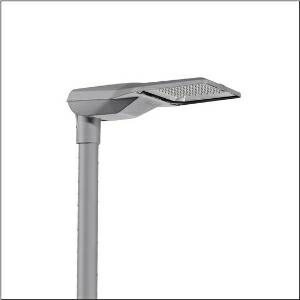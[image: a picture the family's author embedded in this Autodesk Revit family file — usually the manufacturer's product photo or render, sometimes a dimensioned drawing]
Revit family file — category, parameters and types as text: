
# Revit family: streetlight_sl_21_iq_midi___st0_8a_5xe3c41d08mb_0a8a
name_source: partatom
category: Lighting Fixtures
units: mm (PartAtom-declared; Revit-internal decimal feet)

## family parameters
Cut with Voids When Loaded = No
Host = Face
Light Source = No
Part Type = Normal
Room Calculation Point = No
Round Connector Dimension = Use Diameter
Shared = No

## types (1)
- --- (1 x LED, 20360 lm, 146.7 W, 4000K)
    Apparent Load = 147 VA
    CIE Flux Codes = 38 75 97 100 100
    Color Rendering = 70
    Color Temperature = 4000K
    Default Elevation = 1800 mm
    Description = Streetlight SL 21 iQ midi, mast luminaire, primary light control with lens, of PMMA, primary optical cover: cover, of toughened safety glass, transparent, light distribution: ST0.8a, light emission: direct distribution, primary light characteristic: asymmetric, installation type: post-top, side-entry, LED, High Power LED, rated luminous flux: 20.360lm, luminous efficacy: 139lm/W, light colour: 740, colour temperature: 4000K, control gear: iQ-Comfort, control: Auto-Match, Temp-Guard, Lumen-Switch, Night-Set, Smart-Wire, Light-Fading, Desk-Remote (wireless, voltage-free reading and setting of iQ features in the workshop via application-optimized NFC function/RFID function), optimised constant luminous flux control (CLO 2.0), pre-setting: linear dimming characteristic, mains connection: 230..240V, AC, 50/60Hz, start of lifetime: 147W, end of service life: 161W, reduction: 62W, luminaire housing, of diecast aluminium, powder-coated, Siteco® metallic grey (DB 702S), corrosivity category C5 mid according to DIN EN ISO 12944, please order mast flange separately, inclination adjustable: 0°, 5°, 10°, 15°, sealing non-destructively replaceable, multi-level sealing system, length: 644mm, width: 335mm, height: 110mm, mast flange for spigot size: 42mm (side-entry): 5XC10008XM4, 60/48mm (side-entry/post-top): 5XC10108XM2, 76/60mm (side-entry/post-top): 5XC10108XM1, mounting height: 4..8m, protection rating (complete): IP66, insulation class (complete): insulation class II (safety insulation), certification: CE, ENEC, ENEC+, VDE, impact resistance: IK10, permissible operating ambient temperature for outdoor applications: -40..+50°C, standard-compliant lighting for roads and squares, packaging unit: 1 piece

Light Distribution: ST0.8a
    Height = 111 mm
    Lamp = 1 x LED
    Lamp Light Flux = 20360 lm
    Lamp Power = 146.7 W
    Lamp count = 1
    Length = 644 mm
    Luminous efficacy = 139 lm/W
    Manufacturer = Siteco
    ModVariant = No
    Model = 5XE3C41D08MB
    Number of Poles = 1
    OnlyDefault = Yes
    Power Factor = 1
    Product Name = Streetlight SL 21 iQ midi | ST0.8a
    Product group = mast luminaire | pylon top
    ProductGroupID = 6100
    Protection Class = Protection class II
    Protection Degree = IP 66
    RLX_Detail_Level = 1
    RLX_Emergency_Light_Flux = 0 lm
    RLX_Emergency_Type = 0
    RLX_Emergency_Type_DB = No
    RlxData = <blob elided: 27025 chars, md5=76693266>
    Socket = socket
    Standby Power = 0 W
    System Light Flux = 20360 lm
    System Power = 147 W
    Type Comments = factory setting: luminous flux: 100 % | dim-lin: 254 | 753 mA
    Type Image = l_1004298.jpg
    URL = http://relux.com
    VarID = @adj_207481
    Voltage = 0 V
    Weight = 0.00 kg
    Width = 336 mm

## geometry (parser evidence)
native form markers: Blend x4, Sweep x12
no freeform markers — native parametric forms only
